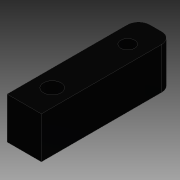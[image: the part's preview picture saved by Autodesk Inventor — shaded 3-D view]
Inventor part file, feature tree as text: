
AUTODESK INVENTOR PART (.ipt)
format: ipt  version: 2015 (Build 190159000, 159)  size: 107,520 bytes
history: native  units: in
note: dims shown in document units (in); Inventor stores cm internally (conversion verified against a paired STEP export)
features: sketch x2, extrude x1, hole x1
ambient origin geometry x8: Origin, YZ Plane, XZ Plane, XY Plane, X Axis, Y Axis, Z Axis, Center Point
bodies: Solid1 (feature_tree)
feature tree (4):
  extrude  "Extrusion1"  Depth=1.225in
  hole  "Hole1"  [1 undecoded]
  sketch  "Sketch1"  dims[d0=4.7in d1=1.225in]
  sketch  "Sketch2"  dims[d2=0.4in d3=0.625in d4=1.0in d5=1.485in d6=0.0in d7=1.0in d8=0.5in d9=0.75in d10=0.375in d11=0.25in d12=0.5635in d13=1.0in d14=0.8108in]
note: 1 required parameter value undecoded (feature->parameter linkage not recoverable at this tier; creation-order binding heuristic only, values carry confidence <= 0.55)
